AUTODESK INVENTOR PART (.ipt)
format: ipt  version: 2015 (Build 190159000, 159)  size: 80,896 bytes
history: native  units: in
note: dims shown in document units (in); Inventor stores cm internally (conversion verified against a paired STEP export)
features: sketch x1
ambient origin geometry x8: Origin, YZ Plane, XZ Plane, XY Plane, X Axis, Y Axis, Z Axis, Center Point
feature tree (1):
  sketch  "Sketch1"  dims[d32=0.75in d33=0.5in d34=0.125in d36=0.1in d37=0.1in d38=0.08in d39=0.08in d40=0.05in d41=90.0deg d42=0.05in d43=0.05in d44=0.05in d45=90.0deg d46=0.05in]
